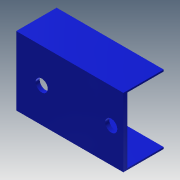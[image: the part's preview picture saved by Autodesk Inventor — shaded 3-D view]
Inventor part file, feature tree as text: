
AUTODESK INVENTOR PART (.ipt)
format: ipt  version: 2015 (Build 190159000, 159)  size: 160,256 bytes
history: native  units: mm
features: extrude x9, sketch x9
ambient origin geometry x8: Origin, YZ Plane, XZ Plane, XY Plane, X Axis, Y Axis, Z Axis, Center Point
bodies: Solid1 (feature_tree)
feature tree (18):
  extrude  "Extrusion1"  Depth=17.0mm
  extrude  "Extrusion2"  Depth=10.0mm
  extrude  "Extrusion3"  Depth=9.0mm TaperAngle=0.0deg
  extrude  "Extrusion4"  Depth=3.0mm
  extrude  "Extrusion5"  Depth=3.0mm
  extrude  "Extrusion6"  Depth=1.0mm TaperAngle=0.0deg
  extrude  "Extrusion7"  Depth=2.0mm
  extrude  "Extrusion8"  Depth=3.0mm
  extrude  "Extrusion9"  Depth=1.0mm
  sketch  "Sketch1"  dims[d0=24.7mm d1=17.0mm]
  sketch  "Sketch2"  dims[d2=10.0mm d3=0.0mm d4=24.7mm]
  sketch  "Sketch3"  dims[d5=16.2mm d6=9.0mm d7=0.0mm]
  sketch  "Sketch4"  dims[d8=3.0mm d9=3.0mm]
  sketch  "Sketch5"  dims[d10=3.0mm d11=3.0mm]
  sketch  "Sketch6"  dims[d12=1.0mm d13=0.0mm d14=2.0mm d15=0.0mm]
  sketch  "Sketch7"  dims[d16=0.2mm d17=0.0mm d18=2.0mm]
  sketch  "Sketch8"  dims[d19=2.0mm d20=3.0mm]
  sketch  "Sketch9"  dims[d21=1.0mm d22=0.0mm d29=3.3mm d30=3.0mm d31=3.0mm d32=1.0mm d33=0.0mm d34=0.1mm d35=0.1mm d36=1.0mm d37=0.0mm d38=3.0mm d39=3.0mm d40=1.0mm d41=0.0mm]
